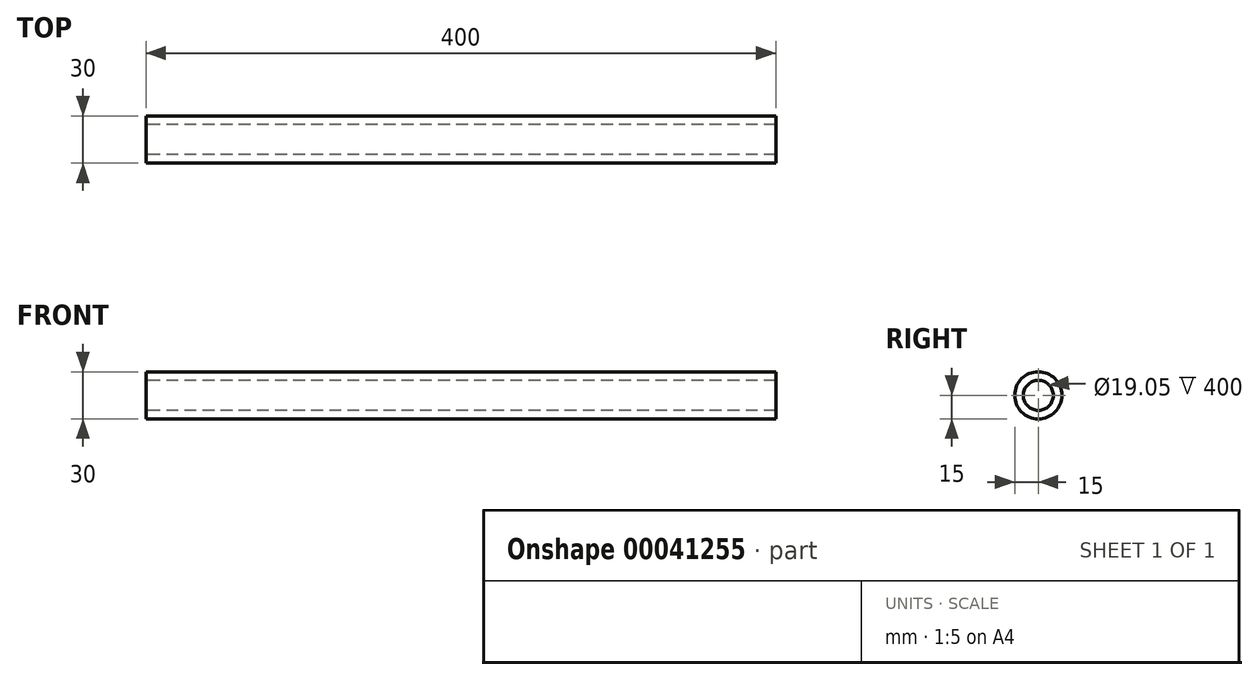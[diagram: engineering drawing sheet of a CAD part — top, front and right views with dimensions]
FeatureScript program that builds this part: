
annotation { "Feature Type Name" : "Feature", "Feature Type Description" : "" }
export const myFeature = defineFeature(function(context is Context, id is Id, definition is map)
    precondition{}
    {
        {
            var Q0;
            Q0=qCreatedBy(makeId("Front.planeOp"),FACE);
            var sketch = newSketch(context, id + "F0", { "sketchPlane" : qUnion([Q0])});
            skLineSegment(sketch, "E0", {"start": v(0.06, 0) * mm, "end": v(200.06, 0) * mm});
            skLineSegment(sketch, "E1", {"start": v(200.06, 0) * mm, "end": v(-199.94, 0) * mm});
            skLineSegment(sketch, "E2", {"start": v(-199.94, 15) * mm, "end": v(200.06, 15) * mm});
            skLineSegment(sketch, "E3", {"start": v(200.06, 0) * mm, "end": v(200.06, 15) * mm});
            skLineSegment(sketch, "E4", {"start": v(-199.94, 15) * mm, "end": v(-199.94, 0) * mm});
            skSolve(sketch);
        }
        {
            var Q0;
            Q0=makeQuery(id+"F0.imprint","IMPRINT",FACE,{"disambiguationData":[TD([[makeQuery(id+"F0.imprint","IMPRINT",EDGE,{"derivedFrom":sQuery(id+"F0.wireOp",EDGE,"E2")}),-1.0]])]});
            var Q1;
            Q1=sQuery(id+"F0.wireOp",EDGE,"E1");
            revolve(context, id + "F1", {"entities" : qUnion([Q0]), "axis" : qUnion([Q1]), "revolveType" : RevolveType.FULL});
        }
        {
            var Q0;
            Q0=makeQuery(id+"F1.opRevolve","SWEPT_FACE",FACE,{"disambiguationData":[OSD([sQuery(id+"F0.wireOp",EDGE,"E4")])]});
            var sketch = newSketch(context, id + "F2", { "sketchPlane" : qUnion([Q0])});
            skCircle(sketch, "E5", {"center": v(0, 0) * mm, "radius": 9.52 * mm});
            skSolve(sketch);
        }
        {
            var Q0;
            Q0=qSketchRegion(id+"F2",true);
            extrude(context, id + "F3", {"entities" : qUnion([Q0]), "operationType" : NewBodyOperationType.REMOVE, "endBound" : BoundingType.THROUGH_ALL, "oppositeDirection" : true, "depth" : 25 * mm});
        }
    });
